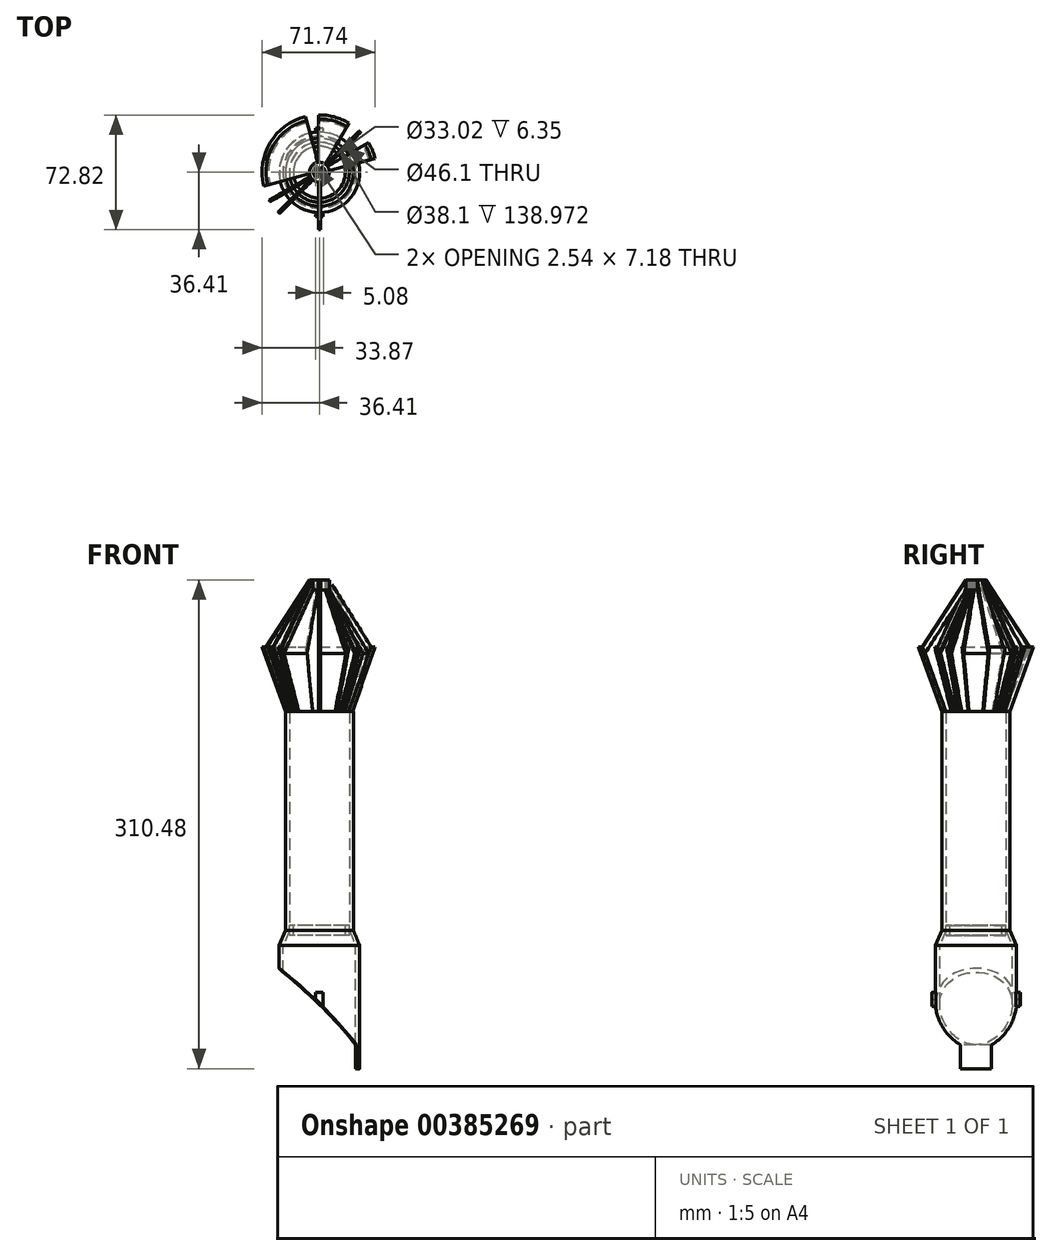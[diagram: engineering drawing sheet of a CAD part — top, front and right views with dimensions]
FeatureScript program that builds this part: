
annotation { "Feature Type Name" : "Feature", "Feature Type Description" : "" }
export const myFeature = defineFeature(function(context is Context, id is Id, definition is map)
    precondition{}
    {
        {
            var Q0;
            Q0=qCreatedBy(makeId("Front.planeOp"),FACE);
            var sketch = newSketch(context, id + "F0", { "sketchPlane" : qUnion([Q0])});
            skLineSegment(sketch, "E0", {"start": v(0, 0) * mm, "end": v(19.05, 0) * mm, "construction": true});
            skLineSegment(sketch, "E1", {"start": v(19.05, 0) * mm, "end": v(21.6, 0) * mm});
            skLineSegment(sketch, "E2", {"start": v(21.59, 0) * mm, "end": v(36.4, 41.08) * mm});
            skLineSegment(sketch, "E3", {"start": v(36.4, 41.08) * mm, "end": v(33.87, 41.08) * mm});
            skLineSegment(sketch, "E4", {"start": v(33.87, 41.08) * mm, "end": v(19.05, 0) * mm});
            skLineSegment(sketch, "E5", {"start": v(19.05, 0) * mm, "end": v(19.05, -138.97) * mm});
            skLineSegment(sketch, "E6", {"start": v(19.05, -138.97) * mm, "end": v(23.05, -148.5) * mm});
            skLineSegment(sketch, "E7", {"start": v(23.05, -148.5) * mm, "end": v(23.05, -226.81) * mm});
            skLineSegment(sketch, "E8", {"start": v(23.05, -226.81) * mm, "end": v(25.6, -226.81) * mm});
            skLineSegment(sketch, "E9", {"start": v(25.6, -226.81) * mm, "end": v(25.6, -148.5) * mm});
            skLineSegment(sketch, "E10", {"start": v(25.6, -148.5) * mm, "end": v(23.05, -148.5) * mm});
            skLineSegment(sketch, "E11", {"start": v(25.6, -148.5) * mm, "end": v(21.6, -138.97) * mm});
            skLineSegment(sketch, "E12", {"start": v(21.6, -138.97) * mm, "end": v(21.6, 0) * mm});
            skLineSegment(sketch, "E13", {"start": v(0, 0) * mm, "end": v(0, -138.97) * mm, "construction": true});
            skLineSegment(sketch, "E14", {"start": v(0, -138.97) * mm, "end": v(19.05, -138.97) * mm, "construction": true});
            skLineSegment(sketch, "E15", {"start": v(0, -138.97) * mm, "end": v(0, -148.5) * mm, "construction": true});
            skLineSegment(sketch, "E16", {"start": v(0, -148.5) * mm, "end": v(23.05, -148.5) * mm, "construction": true});
            skLineSegment(sketch, "E17", {"start": v(0, -148.5) * mm, "end": v(0, -226.81) * mm, "construction": true});
            skLineSegment(sketch, "E18", {"start": v(0, -226.81) * mm, "end": v(23.05, -226.81) * mm, "construction": true});
            skLineSegment(sketch, "E19", {"start": v(19.05, -138.97) * mm, "end": v(21.6, -138.97) * mm});
            skLineSegment(sketch, "E20", {"start": v(0, 0) * mm, "end": v(0, 41.08) * mm, "construction": true});
            skLineSegment(sketch, "E21", {"start": v(0, 41.08) * mm, "end": v(33.87, 41.08) * mm, "construction": true});
            skLineSegment(sketch, "E22", {"start": v(19.05, -135.8) * mm, "end": v(16.51, -135.8) * mm});
            skLineSegment(sketch, "E23", {"start": v(16.51, -135.8) * mm, "end": v(16.51, -142.15) * mm});
            skLineSegment(sketch, "E24", {"start": v(16.51, -142.15) * mm, "end": v(19.05, -142.15) * mm});
            skLineSegment(sketch, "E25", {"start": v(19.05, -142.15) * mm, "end": v(19.05, -135.8) * mm});
            skLineSegment(sketch, "E26", {"start": v(25.6, -154.41) * mm, "end": v(28.13, -154.41) * mm});
            skLineSegment(sketch, "E27", {"start": v(28.13, -154.41) * mm, "end": v(28.13, -226.81) * mm});
            skPoint(sketch, "E28.endSnap0", {"position": v(9.53, 0) * mm});
            skLineSegment(sketch, "E29", {"start": v(101.6, -20.3) * mm, "end": v(101.6, -290.18) * mm, "construction": true});
            skLineSegment(sketch, "E30", {"start": v(101.6, -290.18) * mm, "end": v(0, -188.58) * mm});
            skLineSegment(sketch, "E31", {"start": v(-168.28, -20.3) * mm, "end": v(0, -188.58) * mm});
            skLineSegment(sketch, "E32", {"start": v(0, 41.08) * mm, "end": v(-168.28, 41.08) * mm, "construction": true});
            skPoint(sketch, "E32.endSnap0", {"position": v(16.93, 41.08) * mm});
            skLineSegment(sketch, "E33", {"start": v(-168.28, 41.08) * mm, "end": v(-168.28, -20.3) * mm, "construction": true});
            skLineSegment(sketch, "E34", {"start": v(-168.27, -20.3) * mm, "end": v(101.6, -20.3) * mm, "construction": true});
            skLineSegment(sketch, "E35", {"start": v(-168.27, -20.3) * mm, "end": v(-168.27, -290.18) * mm});
            skLineSegment(sketch, "E36", {"start": v(-168.27, -290.18) * mm, "end": v(101.6, -290.18) * mm});
            skLineSegment(sketch, "E37", {"start": v(0, -188.58) * mm, "end": v(28.13, -188.58) * mm, "construction": true});
            skLineSegment(sketch, "E38", {"start": v(25.6, -188.58) * mm, "end": v(28.13, -188.58) * mm, "construction": true});
            skLineSegment(sketch, "E39", {"start": v(26.86, -188.58) * mm, "end": v(26.86, -226.81) * mm, "construction": true});
            skLineSegment(sketch, "E40", {"start": v(26.86, -188.58) * mm, "end": v(26.86, -178.42) * mm, "construction": true});
            skLineSegment(sketch, "E41", {"start": v(25.6, -178.42) * mm, "end": v(28.13, -178.42) * mm});
            skLineSegment(sketch, "E42", {"start": v(25.6, -226.81) * mm, "end": v(28.13, -226.81) * mm});
            skLineSegment(sketch, "E43", {"start": v(0, 41.08) * mm, "end": v(0, 83.67) * mm, "construction": true});
            skLineSegment(sketch, "E44", {"start": v(0, 83.67) * mm, "end": v(6.35, 83.67) * mm});
            skLineSegment(sketch, "E45", {"start": v(6.35, 83.67) * mm, "end": v(6.35, 77.32) * mm});
            skLineSegment(sketch, "E46", {"start": v(6.35, 77.32) * mm, "end": v(0, 77.32) * mm});
            skLineSegment(sketch, "E47", {"start": v(6.35, 77.32) * mm, "end": v(32.4, 37) * mm});
            skLineSegment(sketch, "E48", {"start": v(6.35, 83.67) * mm, "end": v(33.87, 41.08) * mm});
            skLineSegment(sketch, "E49", {"start": v(3.81, 83.67) * mm, "end": v(3.81, 77.32) * mm});
            skSolve(sketch);
        }
        {
            var Q0;
            Q0=makeQuery(id+"F0.imprint","IMPRINT",FACE,{"disambiguationData":[TD([[makeQuery(id+"F0.imprint","IMPRINT",EDGE,{"derivedFrom":sQuery(id+"F0.wireOp",EDGE,"E1")}),1.0]])]});
            var Q1;
            Q1=makeQuery(id+"F0.imprint","IMPRINT",FACE,{"disambiguationData":[TD([[makeQuery(id+"F0.imprint","IMPRINT",EDGE,{"derivedFrom":sQuery(id+"F0.wireOp",EDGE,"E1")}),-1.0]])]});
            var Q2;
            Q2=sQuery(id+"F0.wireOp",EDGE,"E20");
            revolve(context, id + "F1", {"entities" : qUnion([Q0, Q1]), "axis" : qUnion([Q2]), "revolveType" : RevolveType.FULL});
        }
        {
            var Q0;
            {var subQ3=sQuery(id+"F0.wireOp",EDGE,"E22");Q0=makeQuery(id+"F0.imprint","IMPRINT",FACE,{"disambiguationData":[TD([[makeQuery(id+"F0.imprint","IMPRINT",EDGE,{"derivedFrom":subQ3}),1.0]])]});}
            var Q1;
            Q1=sQuery(id+"F0.wireOp",EDGE,"E15");
            revolve(context, id + "F2", {"entities" : qUnion([Q0]), "axis" : qUnion([Q1]), "revolveType" : RevolveType.FULL});
        }
        {
            var Q0;
            Q0=makeQuery(id+"F0.imprint","IMPRINT",FACE,{"disambiguationData":[TD([[makeQuery(id+"F0.imprint","IMPRINT",EDGE,{"derivedFrom":sQuery(id+"F0.wireOp",EDGE,"E6")}),1.0]])]});
            var Q1;
            Q1=makeQuery(id+"F0.imprint","IMPRINT",FACE,{"disambiguationData":[TD([[makeQuery(id+"F0.imprint","IMPRINT",EDGE,{"derivedFrom":sQuery(id+"F0.wireOp",EDGE,"E7")}),1.0]])]});
            var Q2;
            {var subQ0=sQuery(id+"F0.wireOp",EDGE,"E10");Q2=makeQuery(id+"F0.imprint","IMPRINT",FACE,{"disambiguationData":[TD([[makeQuery(id+"F0.imprint","IMPRINT",EDGE,{"derivedFrom":subQ0}),1.0]])]});}
            var Q3;
            Q3=sQuery(id+"F0.wireOp",EDGE,"E15");
            revolve(context, id + "F3", {"entities" : qUnion([Q0, Q1, Q2]), "axis" : qUnion([Q3]), "revolveType" : RevolveType.FULL});
        }
        {
            var Q0;
            {var subQ0=sQuery(id+"F0.wireOp",EDGE,"E41");Q0=makeQuery(id+"F0.imprint","IMPRINT",FACE,{"disambiguationData":[TD([[makeQuery(id+"F0.imprint","IMPRINT",EDGE,{"derivedFrom":subQ0}),-1.0]])]});}
            var Q1;
            {var subQ0=sQuery(id+"F0.wireOp",EDGE,"E42");Q1=makeQuery(id+"F0.imprint","IMPRINT",FACE,{"disambiguationData":[TD([[makeQuery(id+"F0.imprint","IMPRINT",EDGE,{"derivedFrom":subQ0}),1.0]])]});}
            var Q2;
            Q2=sQuery(id+"F0.wireOp",EDGE,"E17");
            revolve(context, id + "F4", {"entities" : qUnion([Q0, Q1]), "axis" : qUnion([Q2]), "revolveType" : RevolveType.TWO_DIRECTIONS, "angle" : 95 * degree, "angleBack" : 85 * degree});
        }
        {
            var Q0;
            {var subQ0=sQuery(id+"F0.wireOp",EDGE,"E41");Q0=makeQuery(id+"F0.imprint","IMPRINT",FACE,{"disambiguationData":[TD([[makeQuery(id+"F0.imprint","IMPRINT",EDGE,{"derivedFrom":subQ0}),-1.0]])]});}
            var Q1;
            {var subQ0=sQuery(id+"F0.wireOp",EDGE,"E42");Q1=makeQuery(id+"F0.imprint","IMPRINT",FACE,{"disambiguationData":[TD([[makeQuery(id+"F0.imprint","IMPRINT",EDGE,{"derivedFrom":subQ0}),1.0]])]});}
            var Q2;
            Q2=sQuery(id+"F0.wireOp",EDGE,"E17");
            revolve(context, id + "F5", {"entities" : qUnion([Q0, Q1]), "axis" : qUnion([Q2]), "revolveType" : RevolveType.TWO_DIRECTIONS, "angle" : 275 * degree, "angleBack" : 265 * degree});
        }
        {
            var Q0;
            {var subQ5=sQuery(id+"F0.wireOp",EDGE,"E8");Q0=makeQuery(id+"F0.imprint","IMPRINT",FACE,{"disambiguationData":[TD([[makeQuery(id+"F0.imprint","IMPRINT",EDGE,{"derivedFrom":subQ5}),-1.0]])]});}
            var Q1;
            Q1=sQuery(id+"F0.wireOp",EDGE,"E29");
            revolve(context, id + "F6", {"operationType" : NewBodyOperationType.REMOVE, "entities" : qUnion([Q0]), "axis" : qUnion([Q1]), "revolveType" : RevolveType.TWO_DIRECTIONS, "angle" : 30 * degree, "angleBack" : 330 * degree});
        }
        {
            var Q0;
            Q0=makeQuery(id+"F0.imprint","IMPRINT",FACE,{"disambiguationData":[TD([[makeQuery(id+"F0.imprint","IMPRINT",EDGE,{"derivedFrom":sQuery(id+"F0.wireOp",EDGE,"E45")}),1.0]])]});
            var Q1;
            {var subQ0=sQuery(id+"F0.wireOp",EDGE,"E45");Q1=makeQuery(id+"F0.imprint","IMPRINT",FACE,{"disambiguationData":[TD([[makeQuery(id+"F0.imprint","IMPRINT",EDGE,{"derivedFrom":subQ0}),-1.0]])]});}
            var Q2;
            Q2=sQuery(id+"F0.wireOp",EDGE,"E43");
            revolve(context, id + "F7", {"entities" : qUnion([Q0, Q1]), "axis" : qUnion([Q2]), "revolveType" : RevolveType.FULL});
        }
        {
            var Q0;
            Q0=qCreatedBy(makeId("Top.planeOp"),FACE);
            var sketch = newSketch(context, id + "F8", { "sketchPlane" : qUnion([Q0])});
            skCircle(sketch, "E50", {"center": v(0, 0) * mm, "radius": 36.4 * mm});
            skCircle(sketch, "E51", {"center": v(0, 0) * mm, "radius": 6.35 * mm});
            skLineSegment(sketch, "E52", {"start": v(0, 0) * mm, "end": v(-36.4, 0) * mm, "construction": true});
            skLineSegment(sketch, "E53", {"start": v(0, 0) * mm, "end": v(0, 36.4) * mm, "construction": true});
            skLineSegment(sketch, "E54", {"start": v(0, 0) * mm, "end": v(36.4, 0) * mm, "construction": true});
            skLineSegment(sketch, "E55", {"start": v(0, 0) * mm, "end": v(0, -36.4) * mm, "construction": true});
            skLineSegment(sketch, "E56", {"start": v(0, 0) * mm, "end": v(-35.17, 9.42) * mm, "construction": true});
            skLineSegment(sketch, "E57", {"start": v(0, 0) * mm, "end": v(-31.53, 18.2) * mm, "construction": true});
            skLineSegment(sketch, "E58", {"start": v(0, 0) * mm, "end": v(-25.74, 25.74) * mm, "construction": true});
            skLineSegment(sketch, "E59", {"start": v(0, 0) * mm, "end": v(-18.2, 31.53) * mm, "construction": true});
            skLineSegment(sketch, "E60", {"start": v(0, 0) * mm, "end": v(-9.42, 35.17) * mm, "construction": true});
            skLineSegment(sketch, "E61", {"start": v(0, 0) * mm, "end": v(9.42, 35.17) * mm, "construction": true});
            skLineSegment(sketch, "E62", {"start": v(0, 0) * mm, "end": v(18.2, 31.53) * mm, "construction": true});
            skLineSegment(sketch, "E63", {"start": v(0, 0) * mm, "end": v(25.74, 25.74) * mm, "construction": true});
            skLineSegment(sketch, "E64", {"start": v(0, 0) * mm, "end": v(31.53, 18.2) * mm, "construction": true});
            skLineSegment(sketch, "E65", {"start": v(0, 0) * mm, "end": v(35.17, 9.42) * mm, "construction": true});
            skLineSegment(sketch, "E66", {"start": v(0, 0) * mm, "end": v(35.17, -9.42) * mm, "construction": true});
            skLineSegment(sketch, "E67", {"start": v(0, 0) * mm, "end": v(31.53, -18.2) * mm, "construction": true});
            skLineSegment(sketch, "E68", {"start": v(0, 0) * mm, "end": v(25.74, -25.74) * mm, "construction": true});
            skLineSegment(sketch, "E69", {"start": v(0, 0) * mm, "end": v(18.2, -31.53) * mm, "construction": true});
            skLineSegment(sketch, "E70", {"start": v(0, 0) * mm, "end": v(9.42, -35.17) * mm, "construction": true});
            skLineSegment(sketch, "E71", {"start": v(0, 0) * mm, "end": v(-9.42, -35.17) * mm, "construction": true});
            skLineSegment(sketch, "E72", {"start": v(0, 0) * mm, "end": v(-18.2, -31.53) * mm, "construction": true});
            skLineSegment(sketch, "E73", {"start": v(0, 0) * mm, "end": v(-25.74, -25.74) * mm, "construction": true});
            skLineSegment(sketch, "E74", {"start": v(0, 0) * mm, "end": v(-31.53, -18.2) * mm, "construction": true});
            skLineSegment(sketch, "E75", {"start": v(0, 0) * mm, "end": v(-35.17, -9.42) * mm, "construction": true});
            skLineSegment(sketch, "E76", {"start": v(-36.4, 0) * mm, "end": v(-36.4, 0.64) * mm});
            skLineSegment(sketch, "E77", {"start": v(-36.4, 0.64) * mm, "end": v(36.4, 0.64) * mm});
            skLineSegment(sketch, "E78", {"start": v(36.4, 0.64) * mm, "end": v(36.4, -0.64) * mm});
            skLineSegment(sketch, "E79", {"start": v(36.4, -0.64) * mm, "end": v(-36.4, -0.64) * mm});
            skLineSegment(sketch, "E80", {"start": v(-36.4, -0.64) * mm, "end": v(-36.4, 0) * mm});
            skLineSegment(sketch, "E81", {"start": v(-35.17, 9.42) * mm, "end": v(-35, 10.04) * mm});
            skLineSegment(sketch, "E82", {"start": v(-35, 10.04) * mm, "end": v(35.33, -8.8) * mm});
            skLineSegment(sketch, "E83", {"start": v(35.33, -8.8) * mm, "end": v(35, -10.04) * mm});
            skLineSegment(sketch, "E84", {"start": v(35, -10.04) * mm, "end": v(-35.33, 8.8) * mm});
            skLineSegment(sketch, "E85", {"start": v(-35.33, 8.8) * mm, "end": v(-35.17, 9.42) * mm});
            skLineSegment(sketch, "E86", {"start": v(-31.53, 18.2) * mm, "end": v(-31.21, 18.75) * mm});
            skLineSegment(sketch, "E87", {"start": v(-31.21, 18.75) * mm, "end": v(31.85, -17.65) * mm});
            skLineSegment(sketch, "E88", {"start": v(31.85, -17.65) * mm, "end": v(31.21, -18.75) * mm});
            skLineSegment(sketch, "E89", {"start": v(31.21, -18.75) * mm, "end": v(-31.85, 17.65) * mm});
            skLineSegment(sketch, "E90", {"start": v(-31.85, 17.65) * mm, "end": v(-31.53, 18.2) * mm});
            skLineSegment(sketch, "E91", {"start": v(-25.74, 25.74) * mm, "end": v(-25.3, 26.2) * mm});
            skLineSegment(sketch, "E92", {"start": v(-25.3, 26.2) * mm, "end": v(26.2, -25.3) * mm});
            skLineSegment(sketch, "E93", {"start": v(26.2, -25.3) * mm, "end": v(25.3, -26.2) * mm});
            skLineSegment(sketch, "E94", {"start": v(25.3, -26.2) * mm, "end": v(-26.2, 25.3) * mm});
            skLineSegment(sketch, "E95", {"start": v(-26.2, 25.3) * mm, "end": v(-25.74, 25.74) * mm});
            skLineSegment(sketch, "E96", {"start": v(-18.2, 31.53) * mm, "end": v(-17.65, 31.85) * mm});
            skLineSegment(sketch, "E97", {"start": v(-17.65, 31.85) * mm, "end": v(18.75, -31.21) * mm});
            skLineSegment(sketch, "E98", {"start": v(17.65, -31.85) * mm, "end": v(18.75, -31.21) * mm});
            skLineSegment(sketch, "E99", {"start": v(17.65, -31.85) * mm, "end": v(-18.75, 31.21) * mm});
            skLineSegment(sketch, "E100", {"start": v(-18.75, 31.21) * mm, "end": v(-18.2, 31.53) * mm});
            skLineSegment(sketch, "E101", {"start": v(-9.42, 35.17) * mm, "end": v(-8.8, 35.33) * mm});
            skLineSegment(sketch, "E102", {"start": v(-8.8, 35.33) * mm, "end": v(10.04, -35) * mm});
            skLineSegment(sketch, "E103", {"start": v(10.04, -35) * mm, "end": v(8.8, -35.33) * mm});
            skLineSegment(sketch, "E104", {"start": v(8.8, -35.33) * mm, "end": v(-10.04, 35) * mm});
            skLineSegment(sketch, "E105", {"start": v(-10.04, 35) * mm, "end": v(-9.42, 35.17) * mm});
            skLineSegment(sketch, "E106", {"start": v(0, 36.4) * mm, "end": v(0.63, 36.4) * mm});
            skLineSegment(sketch, "E107", {"start": v(0.63, 36.4) * mm, "end": v(0.64, -36.4) * mm});
            skLineSegment(sketch, "E108", {"start": v(0.64, -36.4) * mm, "end": v(-0.63, -36.4) * mm});
            skLineSegment(sketch, "E109", {"start": v(-0.63, -36.4) * mm, "end": v(-0.64, 36.4) * mm});
            skLineSegment(sketch, "E110", {"start": v(-0.63, 36.4) * mm, "end": v(0, 36.4) * mm});
            skLineSegment(sketch, "E111", {"start": v(9.42, 35.17) * mm, "end": v(10.04, 35) * mm});
            skLineSegment(sketch, "E112", {"start": v(10.04, 35) * mm, "end": v(-8.8, -35.33) * mm});
            skLineSegment(sketch, "E113", {"start": v(-8.8, -35.33) * mm, "end": v(-10.04, -35) * mm});
            skLineSegment(sketch, "E114", {"start": v(-10.04, -35) * mm, "end": v(8.8, 35.33) * mm});
            skLineSegment(sketch, "E115", {"start": v(9.42, 35.17) * mm, "end": v(8.8, 35.33) * mm});
            skLineSegment(sketch, "E116", {"start": v(18.2, 31.53) * mm, "end": v(18.75, 31.21) * mm});
            skLineSegment(sketch, "E117", {"start": v(18.75, 31.21) * mm, "end": v(-17.65, -31.85) * mm});
            skLineSegment(sketch, "E118", {"start": v(-17.65, -31.85) * mm, "end": v(-18.75, -31.21) * mm});
            skLineSegment(sketch, "E119", {"start": v(-18.75, -31.21) * mm, "end": v(17.65, 31.85) * mm});
            skLineSegment(sketch, "E120", {"start": v(17.65, 31.85) * mm, "end": v(18.2, 31.53) * mm});
            skLineSegment(sketch, "E121", {"start": v(25.74, 25.74) * mm, "end": v(26.2, 25.3) * mm});
            skLineSegment(sketch, "E122", {"start": v(26.2, 25.3) * mm, "end": v(-25.3, -26.2) * mm});
            skLineSegment(sketch, "E123", {"start": v(-25.3, -26.2) * mm, "end": v(-26.2, -25.3) * mm});
            skLineSegment(sketch, "E124", {"start": v(-26.2, -25.3) * mm, "end": v(25.3, 26.2) * mm});
            skLineSegment(sketch, "E125", {"start": v(25.3, 26.2) * mm, "end": v(25.74, 25.74) * mm});
            skLineSegment(sketch, "E126", {"start": v(31.53, 18.2) * mm, "end": v(31.85, 17.65) * mm});
            skLineSegment(sketch, "E127", {"start": v(31.85, 17.65) * mm, "end": v(-31.21, -18.75) * mm});
            skLineSegment(sketch, "E128", {"start": v(-31.21, -18.75) * mm, "end": v(-31.85, -17.65) * mm});
            skLineSegment(sketch, "E129", {"start": v(-31.85, -17.65) * mm, "end": v(31.21, 18.75) * mm});
            skLineSegment(sketch, "E130", {"start": v(31.21, 18.75) * mm, "end": v(31.53, 18.2) * mm});
            skLineSegment(sketch, "E131", {"start": v(35.17, 9.42) * mm, "end": v(35.33, 8.8) * mm});
            skLineSegment(sketch, "E132", {"start": v(35.33, 8.8) * mm, "end": v(-35, -10.04) * mm});
            skLineSegment(sketch, "E133", {"start": v(35, 10.04) * mm, "end": v(35.17, 9.42) * mm});
            skLineSegment(sketch, "E134", {"start": v(-35, -10.04) * mm, "end": v(-35.33, -8.8) * mm});
            skLineSegment(sketch, "E135", {"start": v(-35.33, -8.8) * mm, "end": v(35, 10.04) * mm});
            skSolve(sketch);
        }
        {
            var Q0;
            {var subQ0=sQuery(id+"F8.wireOp",EDGE,"E84");var subQ1=sQuery(id+"F8.wireOp",EDGE,"E50");var subQ2=makeQuery(id+"F8.imprint","INTERSECT",VERTEX,{"disambiguationData":[OD(0.0)],"derivedFrom":[subQ1,subQ0]});Q0=makeQuery(id+"F8.imprint","IMPRINT",FACE,{"disambiguationData":[TD([[makeQuery(id+"F8.imprint","IMPRINT",EDGE,{"disambiguationData":[TD([[subQ2,-1.0]])],"derivedFrom":subQ1}),1.0]])]});}
            var Q1;
            {var subQ0=sQuery(id+"F8.wireOp",EDGE,"E89");var subQ1=sQuery(id+"F8.wireOp",EDGE,"E50");var subQ2=makeQuery(id+"F8.imprint","INTERSECT",VERTEX,{"disambiguationData":[OD(0.0)],"derivedFrom":[subQ1,subQ0]});Q1=makeQuery(id+"F8.imprint","IMPRINT",FACE,{"disambiguationData":[TD([[makeQuery(id+"F8.imprint","IMPRINT",EDGE,{"disambiguationData":[TD([[subQ2,-1.0]])],"derivedFrom":subQ1}),1.0]])]});}
            var Q2;
            {var subQ0=sQuery(id+"F8.wireOp",EDGE,"E94");var subQ1=sQuery(id+"F8.wireOp",EDGE,"E50");var subQ2=makeQuery(id+"F8.imprint","INTERSECT",VERTEX,{"disambiguationData":[OD(0.0)],"derivedFrom":[subQ1,subQ0]});Q2=makeQuery(id+"F8.imprint","IMPRINT",FACE,{"disambiguationData":[TD([[makeQuery(id+"F8.imprint","IMPRINT",EDGE,{"disambiguationData":[TD([[subQ2,-1.0]])],"derivedFrom":subQ1}),1.0]])]});}
            var Q3;
            {var subQ0=sQuery(id+"F8.wireOp",EDGE,"E99");var subQ1=sQuery(id+"F8.wireOp",EDGE,"E50");var subQ2=makeQuery(id+"F8.imprint","INTERSECT",VERTEX,{"disambiguationData":[OD(0.0)],"derivedFrom":[subQ1,subQ0]});Q3=makeQuery(id+"F8.imprint","IMPRINT",FACE,{"disambiguationData":[TD([[makeQuery(id+"F8.imprint","IMPRINT",EDGE,{"disambiguationData":[TD([[subQ2,-1.0]])],"derivedFrom":subQ1}),1.0]])]});}
            var Q4;
            {var subQ0=sQuery(id+"F8.wireOp",EDGE,"E109");var subQ1=sQuery(id+"F8.wireOp",EDGE,"E50");var subQ2=makeQuery(id+"F8.imprint","INTERSECT",VERTEX,{"disambiguationData":[OD(0.0)],"derivedFrom":[subQ1,subQ0]});Q4=makeQuery(id+"F8.imprint","IMPRINT",FACE,{"disambiguationData":[TD([[makeQuery(id+"F8.imprint","IMPRINT",EDGE,{"disambiguationData":[TD([[subQ2,-1.0]])],"derivedFrom":subQ1}),1.0]])]});}
            var Q5;
            {var subQ0=sQuery(id+"F8.wireOp",EDGE,"E104");var subQ1=sQuery(id+"F8.wireOp",EDGE,"E50");var subQ2=makeQuery(id+"F8.imprint","INTERSECT",VERTEX,{"disambiguationData":[OD(0.0)],"derivedFrom":[subQ1,subQ0]});Q5=makeQuery(id+"F8.imprint","IMPRINT",FACE,{"disambiguationData":[TD([[makeQuery(id+"F8.imprint","IMPRINT",EDGE,{"disambiguationData":[TD([[subQ2,-1.0]])],"derivedFrom":subQ1}),1.0]])]});}
            var Q6;
            {var subQ0=sQuery(id+"F8.wireOp",EDGE,"E114");var subQ1=sQuery(id+"F8.wireOp",EDGE,"E50");var subQ2=makeQuery(id+"F8.imprint","INTERSECT",VERTEX,{"disambiguationData":[OD(0.0)],"derivedFrom":[subQ1,subQ0]});Q6=makeQuery(id+"F8.imprint","IMPRINT",FACE,{"disambiguationData":[TD([[makeQuery(id+"F8.imprint","IMPRINT",EDGE,{"disambiguationData":[TD([[subQ2,-1.0]])],"derivedFrom":subQ1}),1.0]])]});}
            var Q7;
            {var subQ0=sQuery(id+"F8.wireOp",EDGE,"E119");var subQ1=sQuery(id+"F8.wireOp",EDGE,"E50");var subQ2=makeQuery(id+"F8.imprint","INTERSECT",VERTEX,{"disambiguationData":[OD(0.0)],"derivedFrom":[subQ1,subQ0]});Q7=makeQuery(id+"F8.imprint","IMPRINT",FACE,{"disambiguationData":[TD([[makeQuery(id+"F8.imprint","IMPRINT",EDGE,{"disambiguationData":[TD([[subQ2,-1.0]])],"derivedFrom":subQ1}),1.0]])]});}
            var Q8;
            {var subQ0=sQuery(id+"F8.wireOp",EDGE,"E124");var subQ1=sQuery(id+"F8.wireOp",EDGE,"E50");var subQ2=makeQuery(id+"F8.imprint","INTERSECT",VERTEX,{"disambiguationData":[OD(0.0)],"derivedFrom":[subQ1,subQ0]});Q8=makeQuery(id+"F8.imprint","IMPRINT",FACE,{"disambiguationData":[TD([[makeQuery(id+"F8.imprint","IMPRINT",EDGE,{"disambiguationData":[TD([[subQ2,-1.0]])],"derivedFrom":subQ1}),1.0]])]});}
            var Q9;
            {var subQ0=sQuery(id+"F8.wireOp",EDGE,"E129");var subQ1=sQuery(id+"F8.wireOp",EDGE,"E50");var subQ2=makeQuery(id+"F8.imprint","INTERSECT",VERTEX,{"disambiguationData":[OD(0.0)],"derivedFrom":[subQ1,subQ0]});Q9=makeQuery(id+"F8.imprint","IMPRINT",FACE,{"disambiguationData":[TD([[makeQuery(id+"F8.imprint","IMPRINT",EDGE,{"disambiguationData":[TD([[subQ2,-1.0]])],"derivedFrom":subQ1}),1.0]])]});}
            var Q10;
            {var subQ0=sQuery(id+"F8.wireOp",EDGE,"E77");var subQ1=sQuery(id+"F8.wireOp",EDGE,"E50");var subQ2=makeQuery(id+"F8.imprint","INTERSECT",VERTEX,{"disambiguationData":[OD(0.0)],"derivedFrom":[subQ1,subQ0]});Q10=makeQuery(id+"F8.imprint","IMPRINT",FACE,{"disambiguationData":[TD([[makeQuery(id+"F8.imprint","IMPRINT",EDGE,{"disambiguationData":[TD([[subQ2,-1.0]])],"derivedFrom":subQ1}),1.0]])]});}
            var Q11;
            {var subQ0=sQuery(id+"F8.wireOp",EDGE,"E135");var subQ1=sQuery(id+"F8.wireOp",EDGE,"E50");var subQ2=makeQuery(id+"F8.imprint","INTERSECT",VERTEX,{"disambiguationData":[OD(0.0)],"derivedFrom":[subQ1,subQ0]});Q11=makeQuery(id+"F8.imprint","IMPRINT",FACE,{"disambiguationData":[TD([[makeQuery(id+"F8.imprint","IMPRINT",EDGE,{"disambiguationData":[TD([[subQ2,-1.0]])],"derivedFrom":subQ1}),1.0]])]});}
            var Q12;
            {var subQ0=sQuery(id+"F8.wireOp",EDGE,"E82");var subQ1=sQuery(id+"F8.wireOp",EDGE,"E50");var subQ2=makeQuery(id+"F8.imprint","INTERSECT",VERTEX,{"disambiguationData":[OD(1.0)],"derivedFrom":[subQ1,subQ0]});Q12=makeQuery(id+"F8.imprint","IMPRINT",FACE,{"disambiguationData":[TD([[makeQuery(id+"F8.imprint","IMPRINT",EDGE,{"disambiguationData":[TD([[subQ2,-1.0]])],"derivedFrom":subQ1}),1.0]])]});}
            var Q13;
            {var subQ0=sQuery(id+"F8.wireOp",EDGE,"E87");var subQ1=sQuery(id+"F8.wireOp",EDGE,"E50");var subQ2=makeQuery(id+"F8.imprint","INTERSECT",VERTEX,{"disambiguationData":[OD(1.0)],"derivedFrom":[subQ1,subQ0]});Q13=makeQuery(id+"F8.imprint","IMPRINT",FACE,{"disambiguationData":[TD([[makeQuery(id+"F8.imprint","IMPRINT",EDGE,{"disambiguationData":[TD([[subQ2,-1.0]])],"derivedFrom":subQ1}),1.0]])]});}
            var Q14;
            {var subQ0=sQuery(id+"F8.wireOp",EDGE,"E92");var subQ1=sQuery(id+"F8.wireOp",EDGE,"E50");var subQ2=makeQuery(id+"F8.imprint","INTERSECT",VERTEX,{"disambiguationData":[OD(1.0)],"derivedFrom":[subQ1,subQ0]});Q14=makeQuery(id+"F8.imprint","IMPRINT",FACE,{"disambiguationData":[TD([[makeQuery(id+"F8.imprint","IMPRINT",EDGE,{"disambiguationData":[TD([[subQ2,-1.0]])],"derivedFrom":subQ1}),1.0]])]});}
            var Q15;
            {var subQ0=sQuery(id+"F8.wireOp",EDGE,"E97");var subQ1=sQuery(id+"F8.wireOp",EDGE,"E50");var subQ2=makeQuery(id+"F8.imprint","INTERSECT",VERTEX,{"disambiguationData":[OD(1.0)],"derivedFrom":[subQ1,subQ0]});Q15=makeQuery(id+"F8.imprint","IMPRINT",FACE,{"disambiguationData":[TD([[makeQuery(id+"F8.imprint","IMPRINT",EDGE,{"disambiguationData":[TD([[subQ2,-1.0]])],"derivedFrom":subQ1}),1.0]])]});}
            var Q16;
            {var subQ0=sQuery(id+"F8.wireOp",EDGE,"E102");var subQ1=sQuery(id+"F8.wireOp",EDGE,"E50");var subQ2=makeQuery(id+"F8.imprint","INTERSECT",VERTEX,{"disambiguationData":[OD(1.0)],"derivedFrom":[subQ1,subQ0]});Q16=makeQuery(id+"F8.imprint","IMPRINT",FACE,{"disambiguationData":[TD([[makeQuery(id+"F8.imprint","IMPRINT",EDGE,{"disambiguationData":[TD([[subQ2,-1.0]])],"derivedFrom":subQ1}),1.0]])]});}
            var Q17;
            {var subQ0=sQuery(id+"F8.wireOp",EDGE,"E107");var subQ1=sQuery(id+"F8.wireOp",EDGE,"E50");var subQ2=makeQuery(id+"F8.imprint","INTERSECT",VERTEX,{"disambiguationData":[OD(1.0)],"derivedFrom":[subQ1,subQ0]});Q17=makeQuery(id+"F8.imprint","IMPRINT",FACE,{"disambiguationData":[TD([[makeQuery(id+"F8.imprint","IMPRINT",EDGE,{"disambiguationData":[TD([[subQ2,-1.0]])],"derivedFrom":subQ1}),1.0]])]});}
            var Q18;
            {var subQ0=sQuery(id+"F8.wireOp",EDGE,"E112");var subQ1=sQuery(id+"F8.wireOp",EDGE,"E50");var subQ2=makeQuery(id+"F8.imprint","INTERSECT",VERTEX,{"disambiguationData":[OD(1.0)],"derivedFrom":[subQ1,subQ0]});Q18=makeQuery(id+"F8.imprint","IMPRINT",FACE,{"disambiguationData":[TD([[makeQuery(id+"F8.imprint","IMPRINT",EDGE,{"disambiguationData":[TD([[subQ2,-1.0]])],"derivedFrom":subQ1}),1.0]])]});}
            var Q19;
            {var subQ0=sQuery(id+"F8.wireOp",EDGE,"E117");var subQ1=sQuery(id+"F8.wireOp",EDGE,"E50");var subQ2=makeQuery(id+"F8.imprint","INTERSECT",VERTEX,{"disambiguationData":[OD(1.0)],"derivedFrom":[subQ1,subQ0]});Q19=makeQuery(id+"F8.imprint","IMPRINT",FACE,{"disambiguationData":[TD([[makeQuery(id+"F8.imprint","IMPRINT",EDGE,{"disambiguationData":[TD([[subQ2,-1.0]])],"derivedFrom":subQ1}),1.0]])]});}
            var Q20;
            {var subQ0=sQuery(id+"F8.wireOp",EDGE,"E122");var subQ1=sQuery(id+"F8.wireOp",EDGE,"E50");var subQ2=makeQuery(id+"F8.imprint","INTERSECT",VERTEX,{"disambiguationData":[OD(1.0)],"derivedFrom":[subQ1,subQ0]});Q20=makeQuery(id+"F8.imprint","IMPRINT",FACE,{"disambiguationData":[TD([[makeQuery(id+"F8.imprint","IMPRINT",EDGE,{"disambiguationData":[TD([[subQ2,-1.0]])],"derivedFrom":subQ1}),1.0]])]});}
            var Q21;
            {var subQ0=sQuery(id+"F8.wireOp",EDGE,"E127");var subQ1=sQuery(id+"F8.wireOp",EDGE,"E50");var subQ2=makeQuery(id+"F8.imprint","INTERSECT",VERTEX,{"disambiguationData":[OD(1.0)],"derivedFrom":[subQ1,subQ0]});Q21=makeQuery(id+"F8.imprint","IMPRINT",FACE,{"disambiguationData":[TD([[makeQuery(id+"F8.imprint","IMPRINT",EDGE,{"disambiguationData":[TD([[subQ2,-1.0]])],"derivedFrom":subQ1}),1.0]])]});}
            var Q22;
            {var subQ0=sQuery(id+"F8.wireOp",EDGE,"E132");var subQ1=sQuery(id+"F8.wireOp",EDGE,"E50");var subQ2=makeQuery(id+"F8.imprint","INTERSECT",VERTEX,{"disambiguationData":[OD(1.0)],"derivedFrom":[subQ1,subQ0]});Q22=makeQuery(id+"F8.imprint","IMPRINT",FACE,{"disambiguationData":[TD([[makeQuery(id+"F8.imprint","IMPRINT",EDGE,{"disambiguationData":[TD([[subQ2,-1.0]])],"derivedFrom":subQ1}),1.0]])]});}
            var Q23;
            {var subQ0=sQuery(id+"F8.wireOp",EDGE,"E79");var subQ1=sQuery(id+"F8.wireOp",EDGE,"E50");var subQ2=makeQuery(id+"F8.imprint","INTERSECT",VERTEX,{"disambiguationData":[OD(0.0)],"derivedFrom":[subQ1,subQ0]});Q23=makeQuery(id+"F8.imprint","IMPRINT",FACE,{"disambiguationData":[TD([[makeQuery(id+"F8.imprint","IMPRINT",EDGE,{"disambiguationData":[TD([[subQ2,-1.0]])],"derivedFrom":subQ1}),1.0]])]});}
            extrude(context, id + "F9", {"entities" : qUnion([Q0, Q1, Q2, Q3, Q4, Q5, Q6, Q7, Q8, Q9, Q10, Q11, Q12, Q13, Q14, Q15, Q16, Q17, Q18, Q19, Q20, Q21, Q22, Q23]), "operationType" : NewBodyOperationType.REMOVE, "depth" : 101.6 * mm});
        }
        {
            var Q0;
            Q0=makeQuery(id+"F7.opRevolve","SWEPT_FACE",FACE,{"disambiguationData":[OSD([sQuery(id+"F0.wireOp",EDGE,"E44")])]});
            var sketch = newSketch(context, id + "F10", { "sketchPlane" : qUnion([Q0])});
            skLineSegment(sketch, "E136.bottom", {"start": v(-1.27, 6.22) * mm, "end": v(1.27, 6.22) * mm});
            skLineSegment(sketch, "E136.top", {"start": v(-1.27, -6.22) * mm, "end": v(1.27, -6.22) * mm});
            skLineSegment(sketch, "E136.left", {"start": v(-1.27, 6.22) * mm, "end": v(-1.27, -6.22) * mm});
            skLineSegment(sketch, "E136.right", {"start": v(1.27, 6.22) * mm, "end": v(1.27, -6.22) * mm});
            skPoint(sketch, "E136.middle", {"position": v(0, 0) * mm});
            skSolve(sketch);
        }
        {
            var Q0;
            Q0 = qSketchRegion(id + "F10", true);
            extrude(context, id + "F11", {"entities" : qUnion([Q0]), "operationType" : NewBodyOperationType.ADD, "oppositeDirection" : true, "depth" : 6.35 * mm});
        }
    });
